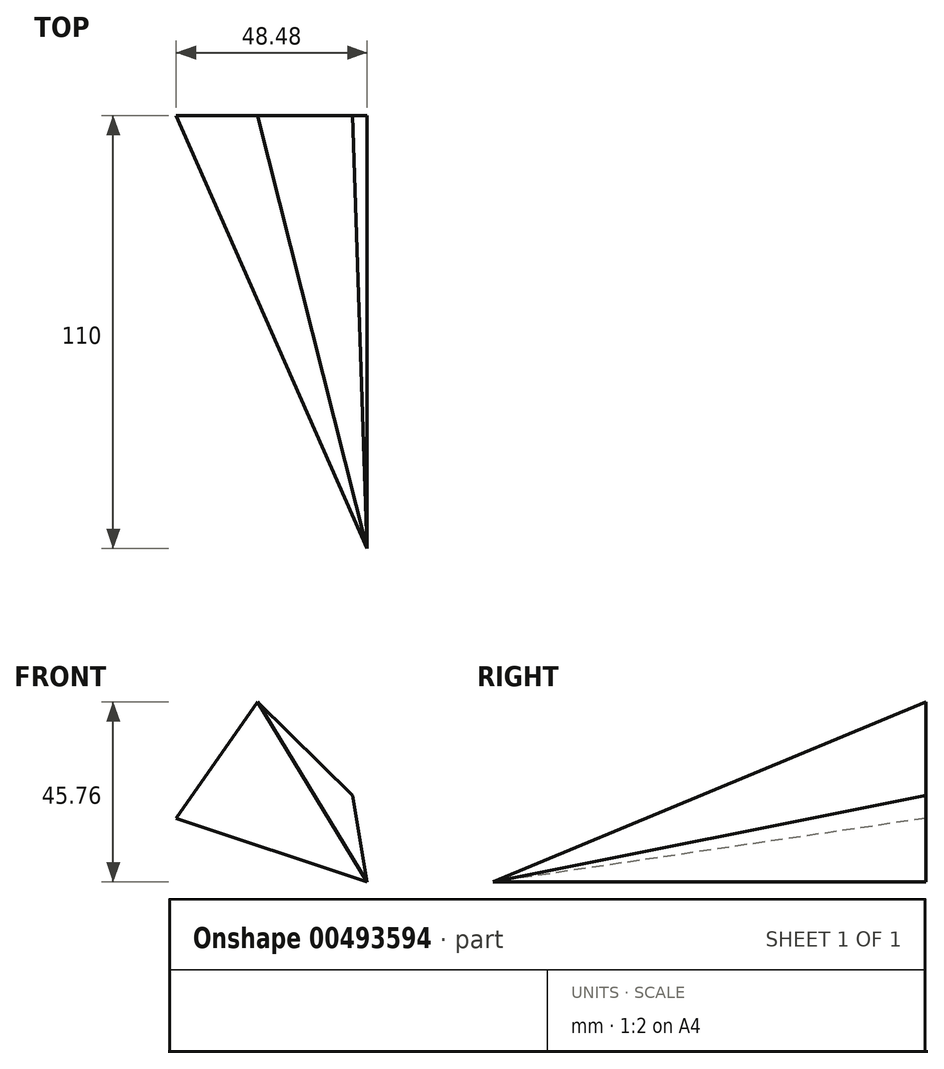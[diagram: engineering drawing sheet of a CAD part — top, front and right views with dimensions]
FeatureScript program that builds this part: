
annotation { "Feature Type Name" : "Feature", "Feature Type Description" : "" }
export const myFeature = defineFeature(function(context is Context, id is Id, definition is map)
    precondition{}
    {
        {
            var Q0;
            Q0=qCreatedBy(makeId("Front.planeOp"),FACE);
            var sketch = newSketch(context, id + "F0", { "sketchPlane" : qUnion([Q0])});
            skLineSegment(sketch, "E0", {"start": v(0, 0) * mm, "end": v(-48.48, 16.2) * mm});
            skLineSegment(sketch, "E1", {"start": v(-48.48, 16.2) * mm, "end": v(-27.83, 45.76) * mm});
            skLineSegment(sketch, "E2", {"start": v(-27.83, 45.76) * mm, "end": v(-3.73, 21.95) * mm});
            skLineSegment(sketch, "E3", {"start": v(-3.73, 21.95) * mm, "end": v(0, 0) * mm});
            skSolve(sketch);
        }
        {
            var Q0;
            Q0=qCreatedBy(makeId("Front.planeOp"),FACE);
            cPlane(context, id + "F1", {"entities" : qUnion([Q0]), "cplaneType" : CPlaneType.OFFSET, "offset" : 110 * mm, "width" : 150 * mm, "height" : 150 * mm});
        }
        {
            var Q0;
            Q0=qCreatedBy(id+"F1.planeOp",FACE);
            var sketch = newSketch(context, id + "F2", { "sketchPlane" : qUnion([Q0])});
            skPoint(sketch, "E4", {"position": v(0, 0) * mm});
            skSolve(sketch);
        }
        {
            var Q0;
            Q0=makeQuery(id+"F0.imprint","IMPRINT",FACE,{"disambiguationData":[TD([[makeQuery(id+"F0.imprint","IMPRINT",EDGE,{"derivedFrom":sQuery(id+"F0.wireOp",EDGE,"E0")}),-1.0]])]});
            var Q1;
            Q1=sQuery(id+"F2.wireOp",VERTEX,"E4");
            loft(context, id + "F3", {"sheetProfilesArray" : [{ "sheetProfileEntities" : qUnion([Q0]) }, { "sheetProfileEntities" : qUnion([Q1]) }]});
        }
    });
